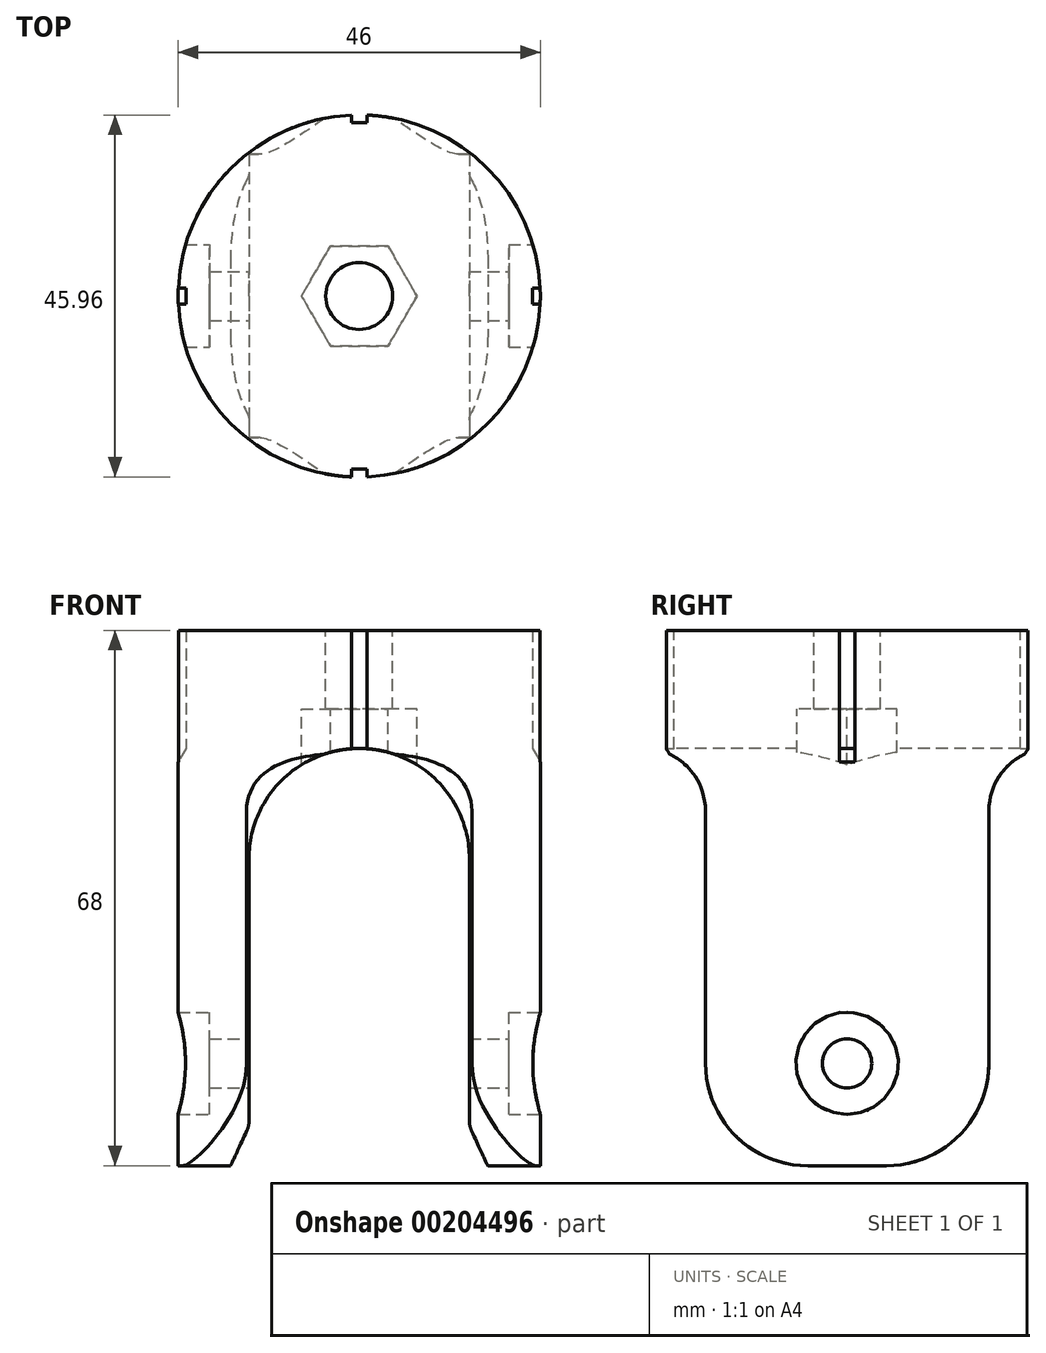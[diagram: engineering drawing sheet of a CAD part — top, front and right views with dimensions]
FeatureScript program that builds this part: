
annotation { "Feature Type Name" : "Feature", "Feature Type Description" : "" }
export const myFeature = defineFeature(function(context is Context, id is Id, definition is map)
    precondition{}
    {
        {
            var Q0;
            Q0=qCreatedBy(makeId("Top.planeOp"),FACE);
            var sketch = newSketch(context, id + "F0", { "sketchPlane" : qUnion([Q0])});
            skCircle(sketch, "E0", {"center": v(0, 0) * mm, "radius": 23 * mm});
            skSolve(sketch);
        }
        {
            var Q0;
            Q0=qSketchRegion(id+"F0",true);
            extrude(context, id + "F1", {"entities" : qUnion([Q0]), "oppositeDirection" : true, "depth" : 68 * mm});
        }
        {
            var Q0;
            Q0=qCreatedBy(makeId("Right.planeOp"),FACE);
            var sketch = newSketch(context, id + "F2", { "sketchPlane" : qUnion([Q0])});
            skCircle(sketch, "E1", {"center": v(0, -55) * mm, "radius": 40 * mm, "construction": true});
            skLineSegment(sketch, "E2", {"start": v(-28, -15) * mm, "end": v(-25, -15) * mm});
            skLineSegment(sketch, "E3", {"start": v(-18, -22.94) * mm, "end": v(-18, -55) * mm});
            skLineSegment(sketch, "E4", {"start": v(-28, -15) * mm, "end": v(-28, -73) * mm});
            skLineSegment(sketch, "E5", {"start": v(-28, -73) * mm, "end": v(0, -73) * mm});
            skLineSegment(sketch, "E6", {"start": v(0, -68) * mm, "end": v(-5, -68) * mm});
            skArc(sketch, "E7", {"start": v(-18, -55) * mm, "mid": v(-14.2, -64.2) * mm, "end": v(-5, -68) * mm});
            skLineSegment(sketch, "E8", {"start": v(0, 0) * mm, "end": v(0, -95) * mm, "construction": true});
            skArc(sketch, "E9", {"start": v(-18, -22.94) * mm, "mid": v(-20, -17.65) * mm, "end": v(-25, -15) * mm});
            skLineSegment(sketch, "E10.MirrorCS", {"start": v(28, -15) * mm, "end": v(25, -15) * mm});
            skArc(sketch, "E11.MirrorCS", {"start": v(18, -22.94) * mm, "mid": v(20, -17.65) * mm, "end": v(25, -15) * mm});
            skArc(sketch, "E12.MirrorCS", {"start": v(18, -55) * mm, "mid": v(14.2, -64.2) * mm, "end": v(5, -68) * mm});
            skLineSegment(sketch, "E13.MirrorCS", {"start": v(0, -68) * mm, "end": v(5, -68) * mm});
            skLineSegment(sketch, "E14.MirrorCS", {"start": v(18, -22.94) * mm, "end": v(18, -55) * mm});
            skLineSegment(sketch, "E15.MirrorCS", {"start": v(28, -73) * mm, "end": v(0, -73) * mm});
            skLineSegment(sketch, "E16.MirrorCS", {"start": v(28, -15) * mm, "end": v(28, -73) * mm});
            skSolve(sketch);
        }
        {
            var Q0;
            Q0=qSketchRegion(id+"F2",true);
            extrude(context, id + "F3", {"entities" : qUnion([Q0]), "operationType" : NewBodyOperationType.REMOVE, "endBound" : BoundingType.THROUGH_ALL, "oppositeDirection" : true, "depth" : 25 * mm, "hasSecondDirection" : true, "secondDirectionBound" : SecondDirectionBoundingType.THROUGH_ALL, "secondDirectionOppositeDirection" : false, "secondDirectionDepth" : 25 * mm});
        }
        {
            var Q0;
            Q0=qCreatedBy(makeId("Front.planeOp"),FACE);
            var sketch = newSketch(context, id + "F4", { "sketchPlane" : qUnion([Q0])});
            skArc(sketch, "E17", {"start": v(14, -29) * mm, "mid": v(0, -15) * mm, "end": v(-14, -29) * mm});
            skLineSegment(sketch, "E18", {"start": v(-14, -29) * mm, "end": v(-14, -62.33) * mm});
            skLineSegment(sketch, "E19", {"start": v(14, -29) * mm, "end": v(14, -62.33) * mm});
            skLineSegment(sketch, "E20", {"start": v(16.33, -68) * mm, "end": v(-16.33, -68) * mm});
            skLineSegment(sketch, "E21", {"start": v(-14.28, -63.6) * mm, "end": v(-16.33, -68) * mm});
            skLineSegment(sketch, "E22", {"start": v(14.28, -63.6) * mm, "end": v(16.33, -68) * mm});
            skLineSegment(sketch, "E23", {"start": v(-14, -63) * mm, "end": v(14, -63) * mm, "construction": true});
            skPoint(sketch, "E24.visualSharp", {"position": v(-14, -63) * mm});
            skArc(sketch, "E24.filletArc", {"start": v(-14.28, -63.6) * mm, "mid": v(-14.07, -62.98) * mm, "end": v(-14, -62.33) * mm});
            skPoint(sketch, "E25.visualSharp", {"position": v(14, -63) * mm});
            skArc(sketch, "E25.filletArc", {"start": v(14, -62.33) * mm, "mid": v(14.07, -62.98) * mm, "end": v(14.28, -63.6) * mm});
            skSolve(sketch);
        }
        {
            var Q0;
            Q0=qSketchRegion(id+"F4",true);
            extrude(context, id + "F5", {"entities" : qUnion([Q0]), "operationType" : NewBodyOperationType.REMOVE, "endBound" : BoundingType.THROUGH_ALL, "oppositeDirection" : true, "depth" : 25 * mm, "hasSecondDirection" : true, "secondDirectionBound" : SecondDirectionBoundingType.THROUGH_ALL, "secondDirectionOppositeDirection" : false, "secondDirectionDepth" : 25 * mm});
        }
        {
            var Q0;
            Q0=qCreatedBy(makeId("Front.planeOp"),FACE);
            var sketch = newSketch(context, id + "F6", { "sketchPlane" : qUnion([Q0])});
            skLineSegment(sketch, "E26", {"start": v(-30.91, -55) * mm, "end": v(31.05, -55) * mm, "construction": true});
            skLineSegment(sketch, "E27", {"start": v(-26, -48.5) * mm, "end": v(-19, -48.5) * mm});
            skLineSegment(sketch, "E28", {"start": v(-19, -48.5) * mm, "end": v(-19, -51.88) * mm});
            skLineSegment(sketch, "E29", {"start": v(-19, -51.88) * mm, "end": v(0, -51.88) * mm});
            skLineSegment(sketch, "E30", {"start": v(-26, -48.5) * mm, "end": v(-26, -55) * mm});
            skLineSegment(sketch, "E31", {"start": v(-26, -55) * mm, "end": v(0, -55) * mm});
            skLineSegment(sketch, "E32.MirrorCS", {"start": v(26, -48.5) * mm, "end": v(19, -48.5) * mm});
            skLineSegment(sketch, "E33.MirrorCS", {"start": v(19, -48.5) * mm, "end": v(19, -51.88) * mm});
            skLineSegment(sketch, "E34.MirrorCS", {"start": v(19, -51.88) * mm, "end": v(0, -51.88) * mm});
            skLineSegment(sketch, "E35.MirrorCS", {"start": v(26, -48.5) * mm, "end": v(26, -55) * mm});
            skLineSegment(sketch, "E36.MirrorCS", {"start": v(26, -55) * mm, "end": v(0, -55) * mm});
            skSolve(sketch);
        }
        {
            var Q0;
            Q0=qSketchRegion(id+"F6",true);
            var Q1;
            Q1=sQuery(id+"F6.wireOp",EDGE,"E26");
            revolve(context, id + "F7", {"operationType" : NewBodyOperationType.REMOVE, "entities" : qUnion([Q0]), "axis" : qUnion([Q1]), "revolveType" : RevolveType.FULL, "oppositeDirection" : true});
        }
        {
            var Q0;
            Q0=makeQuery(id+"F1.opExtrude","CAP_FACE",FACE,{"disambiguationData":[OSD([sQuery(id+"F0.wireOp",EDGE,"E0")])],"isStart":true});
            var sketch = newSketch(context, id + "F8", { "sketchPlane" : qUnion([Q0])});
            skCircle(sketch, "E37", {"center": v(0, 0) * mm, "radius": 4.25 * mm});
            skSolve(sketch);
        }
        {
            var Q0;
            Q0=qSketchRegion(id+"F8",true);
            extrude(context, id + "F9", {"entities" : qUnion([Q0]), "operationType" : NewBodyOperationType.REMOVE, "oppositeDirection" : true, "depth" : 25 * mm});
        }
        {
            var Q0;
            Q0=qCreatedBy(makeId("Top.planeOp"),FACE);
            cPlane(context, id + "F10", {"entities" : qUnion([Q0]), "cplaneType" : CPlaneType.OFFSET, "offset" : 10 * mm, "oppositeDirection" : true, "width" : 150 * mm, "height" : 150 * mm});
        }
        {
            var Q0;
            Q0=qCreatedBy(id+"F10.planeOp",FACE);
            var sketch = newSketch(context, id + "F11", { "sketchPlane" : qUnion([Q0])});
            skCircle(sketch, "E38.cCircle", {"center": v(0, 0) * mm, "radius": 6.35 * mm, "construction": true});
            skLineSegment(sketch, "E38.0", {"start": v(7.33, 0) * mm, "end": v(3.67, -6.35) * mm});
            skLineSegment(sketch, "E38.1", {"start": v(3.67, -6.35) * mm, "end": v(-3.67, -6.35) * mm});
            skLineSegment(sketch, "E38.2", {"start": v(-3.67, -6.35) * mm, "end": v(-7.33, 0) * mm});
            skLineSegment(sketch, "E38.3", {"start": v(-7.33, 0) * mm, "end": v(-3.67, 6.35) * mm});
            skLineSegment(sketch, "E38.4", {"start": v(-3.67, 6.35) * mm, "end": v(3.67, 6.35) * mm});
            skLineSegment(sketch, "E38.5", {"start": v(3.67, 6.35) * mm, "end": v(7.33, 0) * mm});
            skPoint(sketch, "E38.0.midPoint", {"position": v(5.5, -3.18) * mm});
            skSolve(sketch);
        }
        {
            var Q0;
            Q0=qSketchRegion(id+"F11",true);
            extrude(context, id + "F12", {"entities" : qUnion([Q0]), "operationType" : NewBodyOperationType.REMOVE, "oppositeDirection" : true, "depth" : 10 * mm});
        }
        {
            var Q0;
            Q0=makeQuery(id+"F1.opExtrude","CAP_FACE",FACE,{"disambiguationData":[OSD([sQuery(id+"F0.wireOp",EDGE,"E0")])],"isStart":true});
            var sketch = newSketch(context, id + "F13", { "sketchPlane" : qUnion([Q0])});
            skLineSegment(sketch, "E39.bottom", {"start": v(-1, 22) * mm, "end": v(1, 22) * mm});
            skLineSegment(sketch, "E39.top", {"start": v(-1, 24) * mm, "end": v(1, 24) * mm});
            skLineSegment(sketch, "E39.left", {"start": v(-1, 22) * mm, "end": v(-1, 24) * mm});
            skLineSegment(sketch, "E39.right", {"start": v(1, 22) * mm, "end": v(1, 24) * mm});
            skLineSegment(sketch, "E40.bottom", {"start": v(-1, -24) * mm, "end": v(1, -24) * mm});
            skLineSegment(sketch, "E40.top", {"start": v(-1, -22) * mm, "end": v(1, -22) * mm});
            skLineSegment(sketch, "E40.left", {"start": v(-1, -24) * mm, "end": v(-1, -22) * mm});
            skLineSegment(sketch, "E40.right", {"start": v(1, -24) * mm, "end": v(1, -22) * mm});
            skLineSegment(sketch, "E41", {"start": v(0, 18.47) * mm, "end": v(0, -17.11) * mm, "construction": true});
            skPoint(sketch, "E42", {"position": v(0, 22) * mm});
            skPoint(sketch, "E43", {"position": v(0, -22) * mm});
            skSolve(sketch);
        }
        {
            var Q0;
            Q0=qSketchRegion(id+"F13",true);
            extrude(context, id + "F14", {"entities" : qUnion([Q0]), "operationType" : NewBodyOperationType.REMOVE, "oppositeDirection" : true, "depth" : 25 * mm});
        }
        {
            var Q0;
            Q0=qCreatedBy(makeId("Front.planeOp"),FACE);
            var sketch = newSketch(context, id + "F15", { "sketchPlane" : qUnion([Q0])});
            skLineSegment(sketch, "E44", {"start": v(-22, 0) * mm, "end": v(-22, -15) * mm});
            skLineSegment(sketch, "E45", {"start": v(-22, -15) * mm, "end": v(-24, -18.46) * mm});
            skLineSegment(sketch, "E46", {"start": v(-24, -18.46) * mm, "end": v(-25, -18.46) * mm});
            skLineSegment(sketch, "E47", {"start": v(-25, -18.46) * mm, "end": v(-25, 0) * mm});
            skLineSegment(sketch, "E48", {"start": v(-25, 0) * mm, "end": v(-22, 0) * mm});
            skLineSegment(sketch, "E49.MirrorCS", {"start": v(24, -18.46) * mm, "end": v(25, -18.46) * mm});
            skLineSegment(sketch, "E50.MirrorCS", {"start": v(25, 0) * mm, "end": v(22, 0) * mm});
            skLineSegment(sketch, "E51.MirrorCS", {"start": v(22, 0) * mm, "end": v(22, -15) * mm});
            skLineSegment(sketch, "E52.MirrorCS", {"start": v(25, -18.46) * mm, "end": v(25, 0) * mm});
            skLineSegment(sketch, "E53.MirrorCS", {"start": v(22, -15) * mm, "end": v(24, -18.46) * mm});
            skSolve(sketch);
        }
        {
            var Q0;
            Q0 = qSketchRegion(id + "F15", true);
            extrude(context, id + "F16", {"entities" : qUnion([Q0]), "operationType" : NewBodyOperationType.REMOVE, "oppositeDirection" : true, "depth" : 1 * mm, "hasSecondDirection" : true, "secondDirectionOppositeDirection" : false, "secondDirectionDepth" : 1 * mm});
        }
    });
